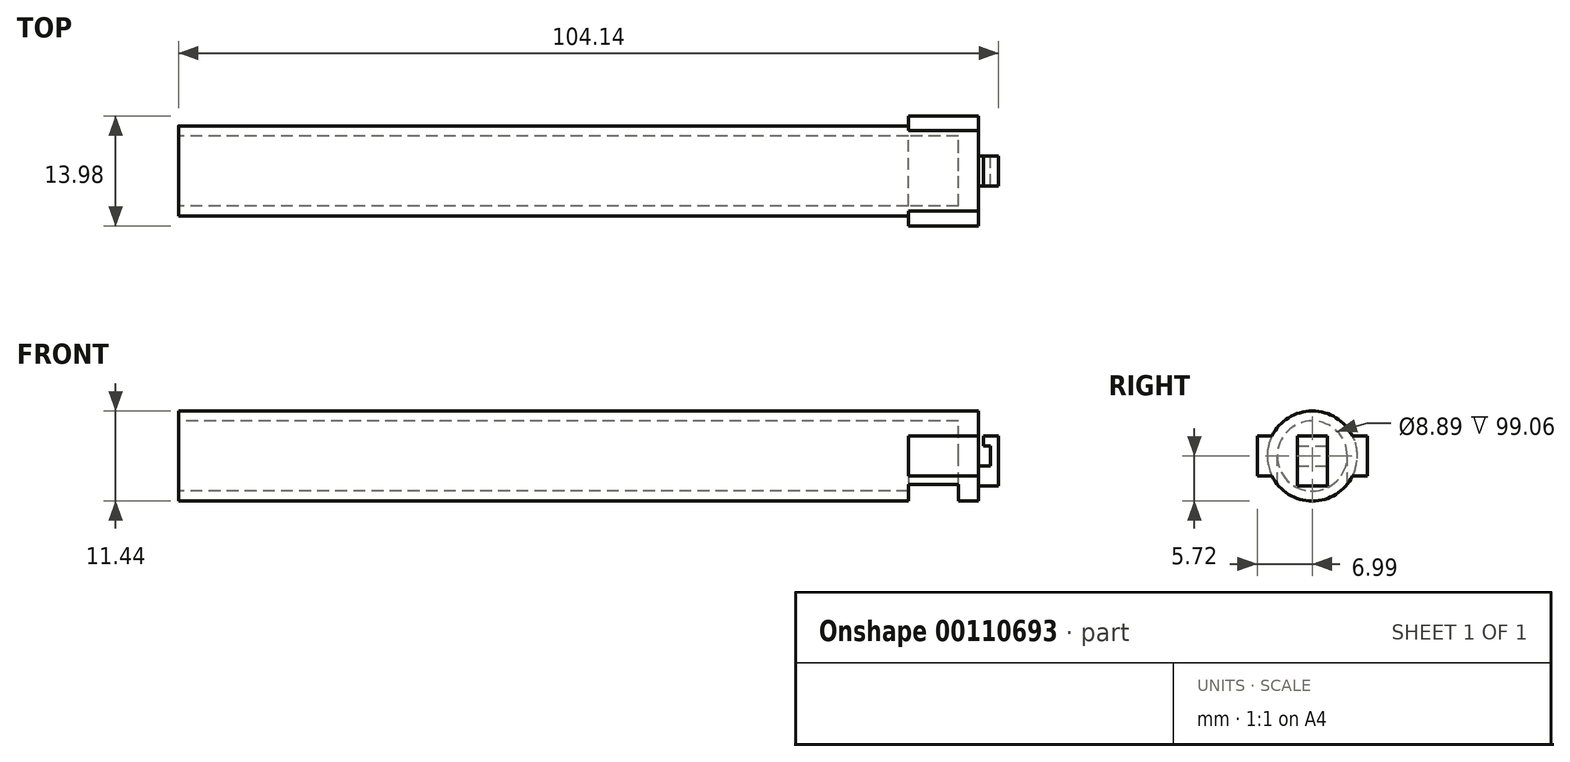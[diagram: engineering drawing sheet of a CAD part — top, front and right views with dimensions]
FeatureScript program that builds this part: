
annotation { "Feature Type Name" : "Feature", "Feature Type Description" : "" }
export const myFeature = defineFeature(function(context is Context, id is Id, definition is map)
    precondition{}
    {
        {
            var Q0;
            Q0=qCreatedBy(makeId("Right.planeOp"),FACE);
            var sketch = newSketch(context, id + "F0", { "sketchPlane" : qUnion([Q0])});
            skCircle(sketch, "E0", {"center": v(0, 0) * mm, "radius": 5.72 * mm});
            skSolve(sketch);
        }
        {
            var Q0;
            Q0 = qSketchRegion(id + "F0", true);
            extrude(context, id + "F1", {"entities" : qUnion([Q0]), "depth" : 101.6 * mm});
        }
        {
            var Q0;
            Q0=makeQuery(id+"F1.opExtrude","CAP_FACE",FACE,{"disambiguationData":[OSD([sQuery(id+"F0.wireOp",EDGE,"E0")])],"isStart":true});
            var sketch = newSketch(context, id + "F2", { "sketchPlane" : qUnion([Q0])});
            skCircle(sketch, "E1", {"center": v(0, 0) * mm, "radius": 4.45 * mm});
            skSolve(sketch);
        }
        {
            var Q0;
            Q0 = qSketchRegion(id + "F2", true);
            extrude(context, id + "F3", {"entities" : qUnion([Q0]), "operationType" : NewBodyOperationType.REMOVE, "oppositeDirection" : true, "depth" : 99.06 * mm});
        }
        {
            var Q0;
            Q0=qCreatedBy(makeId("Top.planeOp"),FACE);
            var sketch = newSketch(context, id + "F4", { "sketchPlane" : qUnion([Q0])});
            skLineSegment(sketch, "E2.bottom", {"start": v(99.06, -4.44) * mm, "end": v(92.71, -4.44) * mm});
            skLineSegment(sketch, "E2.top", {"start": v(99.06, 4.45) * mm, "end": v(92.71, 4.45) * mm});
            skLineSegment(sketch, "E2.left", {"start": v(99.06, -4.44) * mm, "end": v(99.06, 4.45) * mm});
            skLineSegment(sketch, "E2.right", {"start": v(92.71, -4.44) * mm, "end": v(92.71, 4.45) * mm});
            skSolve(sketch);
        }
        {
            var Q0;
            Q0 = qSketchRegion(id + "F4", true);
            extrude(context, id + "F5", {"entities" : qUnion([Q0]), "operationType" : NewBodyOperationType.REMOVE, "oppositeDirection" : true, "depth" : 25.4 * mm});
        }
        {
            var Q0;
            Q0=qCreatedBy(makeId("Right.planeOp"),FACE);
            cPlane(context, id + "F6", {"entities" : qUnion([Q0]), "cplaneType" : CPlaneType.OFFSET, "offset" : 101.6 * mm, "width" : 152.4 * mm, "height" : 152.4 * mm});
        }
        {
            var Q0;
            Q0=qCreatedBy(id+"F6.planeOp",FACE);
            var sketch = newSketch(context, id + "F7", { "sketchPlane" : qUnion([Q0])});
            skLineSegment(sketch, "E3.bottom", {"start": v(5.12, 2.54) * mm, "end": v(6.99, 2.54) * mm});
            skLineSegment(sketch, "E3.top", {"start": v(5.12, -2.54) * mm, "end": v(6.99, -2.54) * mm});
            skLineSegment(sketch, "E3.right", {"start": v(6.99, 2.54) * mm, "end": v(6.99, -2.54) * mm});
            skArc(sketch, "E4", {"start": v(5.12, -2.54) * mm, "mid": v(5.72, 0) * mm, "end": v(5.12, 2.54) * mm});
            skArc(sketch, "E5.MirrorCS", {"start": v(-5.12, -2.54) * mm, "mid": v(-5.72, 0) * mm, "end": v(-5.12, 2.54) * mm});
            skLineSegment(sketch, "E6.MirrorCS", {"start": v(-5.12, 2.54) * mm, "end": v(-6.99, 2.54) * mm});
            skLineSegment(sketch, "E7.MirrorCS", {"start": v(-6.99, 2.54) * mm, "end": v(-6.99, -2.54) * mm});
            skLineSegment(sketch, "E8.MirrorCS", {"start": v(-5.12, -2.54) * mm, "end": v(-6.99, -2.54) * mm});
            skSolve(sketch);
        }
        {
            var Q0;
            Q0 = qSketchRegion(id + "F7", true);
            extrude(context, id + "F8", {"entities" : qUnion([Q0]), "operationType" : NewBodyOperationType.ADD, "oppositeDirection" : true, "depth" : 8.9 * mm});
        }
        {
            var Q0;
            Q0=qCreatedBy(makeId("Front.planeOp"),FACE);
            var sketch = newSketch(context, id + "F9", { "sketchPlane" : qUnion([Q0])});
            skLineSegment(sketch, "E9", {"start": v(103.12, 1.27) * mm, "end": v(102.23, 1.27) * mm});
            skLineSegment(sketch, "E10", {"start": v(102.23, 1.27) * mm, "end": v(102.23, 2.54) * mm});
            skLineSegment(sketch, "E11", {"start": v(102.23, 2.54) * mm, "end": v(104.14, 2.54) * mm});
            skLineSegment(sketch, "E12", {"start": v(104.14, 2.54) * mm, "end": v(104.14, -3.81) * mm});
            skLineSegment(sketch, "E13", {"start": v(104.14, -3.81) * mm, "end": v(101.6, -3.81) * mm});
            skLineSegment(sketch, "E14", {"start": v(101.6, -3.81) * mm, "end": v(101.6, -1.27) * mm});
            skLineSegment(sketch, "E15", {"start": v(101.6, -1.27) * mm, "end": v(103.12, -1.27) * mm});
            skLineSegment(sketch, "E16", {"start": v(103.12, -1.27) * mm, "end": v(103.12, 1.27) * mm});
            skSolve(sketch);
        }
        {
            var Q0;
            Q0 = qSketchRegion(id + "F9", true);
            extrude(context, id + "F10", {"entities" : qUnion([Q0]), "operationType" : NewBodyOperationType.ADD, "depth" : 1.9 * mm, "hasSecondDirection" : true, "secondDirectionOppositeDirection" : true, "secondDirectionDepth" : 1.9 * mm});
        }
    });
